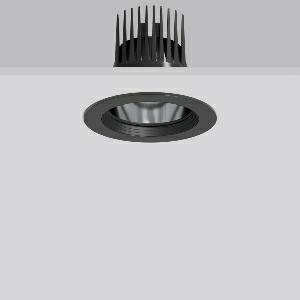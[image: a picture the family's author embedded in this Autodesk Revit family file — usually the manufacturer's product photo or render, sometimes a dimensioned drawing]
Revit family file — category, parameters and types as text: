
# Revit family: heledon_maxi_e_901757_003_76_47bd
name_source: partatom
category: Lighting Fixtures
units: mm (PartAtom-declared; Revit-internal decimal feet)

## family parameters
Cut with Voids When Loaded = No
Host = Face
Light Source = No
Part Type = Normal
Room Calculation Point = No
Round Connector Dimension = Use Diameter
Shared = No

## types (1)
- HELEDON maxi E (1 x LED Modul 930, 3350 lm, 3000)
    Apparent Load = 25 VA
    Approval mark = CE
    CIE Flux Codes = 100 100 100 100 100
    Color Rendering = 90
    Color Temperature = 3000
    Default Elevation = 1800 mm
    Description = Series: HELEDON maxi
Round recessed downlight. Housing: die-cast aluminium, powder-coated. Black plastic ring and recessed LED to prevent glare from the side. Optical assembly with reflector made of MIRO-Silver with 98% total light reflection for outstanding efficiency - can be changed without tools. Best colour rendering index Ra>90. Suitable for Recessed ceiling mounting. Installation without tools thanks to spring fastening system. Including separate LED converter with connecting cable 600 mm.High quality converter without flickering and stroboscopic effect. Through-wiring box (5 pole) available as accessory. The following accessories can be mounted without use of tools: interchangeable lenses, decorative glasses, honeycomb louvre, clear and frosted diffusers, white interchangeable plastic ring. 
Colour: deep black, matt (RAL 9005)
Diameter: 162 mm
Height: 3 mm
Cut-out diameter: 152 mm
Recess height: 200 mm
Luminaire: recess height: 135 mm
Lamp: LED
Socket: without socket
Colour temperature: 3000K
Colour rendering index (CRI): 92
System power: 25 W
Rated luminous flux: 3350 lm
Luminous efficiency: 134 lm/W
Control gear: Converter, dimmable, DALI
Protection class: II
Type of protection: IP 20
    Height = 0 mm  [stored 0 ft]
    Lamp = 1 x LED Modul 930
    Lamp Light Flux = 3350 lm
    Lamp count = 1
    Length = 162 mm
    Lifetime = 50000 h
    Luminous efficacy = 134 lm/W
    Manufacturer = RZB
    ModVariant = No
    Model = 901757.003.76
    Mounting Place = Ceiling
    Mounting Type = Recessed
    Number of Poles = 1
    OnlyDefault = Yes
    Power Factor = 1
    Product Name = HELEDON maxi E
    Product group = Recessed downlights
    ProductGroupID = 402
    Protection Class = Protection class II
    Protection Degree = IP 20
    RLX_Detail_Level = 1
    RLX_Emergency_Light_Flux = 0 lm
    RLX_Emergency_Type = 0
    RLX_Emergency_Type_DB = No
    RlxData = <blob elided: 121241 chars, md5=bc26db14>
    Socket = socket
    Standby Power = 0 W
    System Light Flux = 3350 lm
    System Power = 25 W
    Type Comments = Product without accessories
    Type Image = 901662.003.jpg
    URL = http://relux.com
    VarID = ---
    Voltage = 230 V
    Voltage Range = 220-240 V
    Weight = 0.00 kg
    Width = 0 mm  [stored 0 ft]

note: [stored X ft] marks values corroborated as IEEE doubles in the binary element streams (Revit-internal decimal feet)

## geometry (parser evidence)
native form markers: Blend x4, Sweep x10
no freeform markers — native parametric forms only
